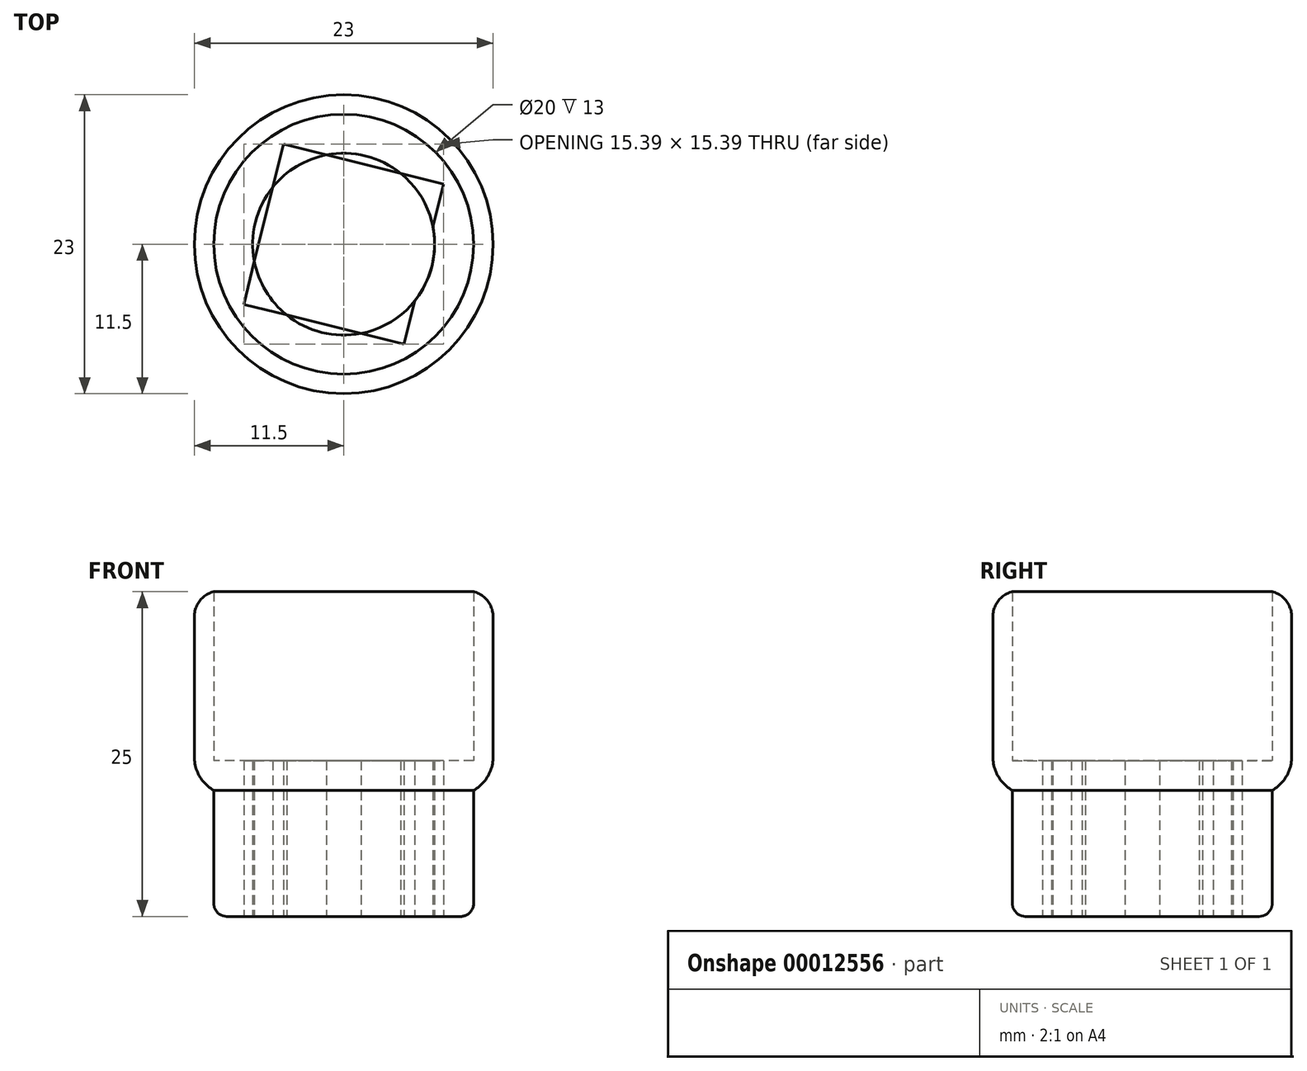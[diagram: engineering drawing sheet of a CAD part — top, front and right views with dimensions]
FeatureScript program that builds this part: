
annotation { "Feature Type Name" : "Feature", "Feature Type Description" : "" }
export const myFeature = defineFeature(function(context is Context, id is Id, definition is map)
    precondition{}
    {
        {
            var Q0;
            Q0=qCreatedBy(makeId("Top.planeOp"),FACE);
            var sketch = newSketch(context, id + "F0", { "sketchPlane" : qUnion([Q0])});
            skCircle(sketch, "E0", {"center": v(0, 0) * mm, "radius": 7 * mm});
            skCircle(sketch, "E1", {"center": v(0, 0) * mm, "radius": 10 * mm});
            skCircle(sketch, "E2", {"center": v(0, 0) * mm, "radius": 11.5 * mm});
            skCircle(sketch, "E3.cCircle", {"center": v(0, 0) * mm, "radius": 8.98 * mm, "construction": true});
            skLineSegment(sketch, "E3.0", {"start": v(7.7, 4.63) * mm, "end": v(4.63, -7.7) * mm});
            skLineSegment(sketch, "E3.1", {"start": v(4.63, -7.7) * mm, "end": v(-7.7, -4.63) * mm});
            skLineSegment(sketch, "E3.2", {"start": v(-7.7, -4.63) * mm, "end": v(-4.63, 7.7) * mm});
            skLineSegment(sketch, "E3.3", {"start": v(-4.63, 7.7) * mm, "end": v(7.7, 4.63) * mm});
            skSolve(sketch);
        }
        {
            var Q0;
            Q0=makeQuery(id+"F0.imprint","IMPRINT",FACE,{"disambiguationData":[TD([[makeQuery(id+"F0.imprint","IMPRINT",EDGE,{"derivedFrom":sQuery(id+"F0.wireOp",EDGE,"E1")}),1.0]])]});
            var Q1;
            {var subQ0=sQuery(id+"F0.wireOp",EDGE,"E3.3");var subQ1=sQuery(id+"F0.wireOp",EDGE,"E0");var subQ2=makeQuery(id+"F0.imprint","INTERSECT",VERTEX,{"disambiguationData":[OD(1.0)],"derivedFrom":[subQ1,subQ0]});Q1=makeQuery(id+"F0.imprint","IMPRINT",FACE,{"disambiguationData":[TD([[makeQuery(id+"F0.imprint","IMPRINT",EDGE,{"disambiguationData":[TD([[subQ2,-1.0]])],"derivedFrom":subQ1}),-1.0]])]});}
            var Q2;
            {var subQ0=sQuery(id+"F0.wireOp",EDGE,"E3.3");var subQ1=sQuery(id+"F0.wireOp",EDGE,"E0");var subQ2=makeQuery(id+"F0.imprint","INTERSECT",VERTEX,{"disambiguationData":[OD(0.0)],"derivedFrom":[subQ1,subQ0]});Q2=makeQuery(id+"F0.imprint","IMPRINT",FACE,{"disambiguationData":[TD([[makeQuery(id+"F0.imprint","IMPRINT",EDGE,{"disambiguationData":[TD([[subQ2,1.0]])],"derivedFrom":subQ1}),-1.0]])]});}
            var Q3;
            {var subQ0=sQuery(id+"F0.wireOp",EDGE,"E3.2");var subQ1=sQuery(id+"F0.wireOp",EDGE,"E0");var subQ2=makeQuery(id+"F0.imprint","INTERSECT",VERTEX,{"disambiguationData":[OD(1.0)],"derivedFrom":[subQ1,subQ0]});Q3=makeQuery(id+"F0.imprint","IMPRINT",FACE,{"disambiguationData":[TD([[makeQuery(id+"F0.imprint","IMPRINT",EDGE,{"disambiguationData":[TD([[subQ2,-1.0]])],"derivedFrom":subQ1}),-1.0]])]});}
            var Q4;
            {var subQ0=sQuery(id+"F0.wireOp",EDGE,"E3.1");var subQ1=sQuery(id+"F0.wireOp",EDGE,"E0");var subQ2=makeQuery(id+"F0.imprint","INTERSECT",VERTEX,{"disambiguationData":[OD(1.0)],"derivedFrom":[subQ1,subQ0]});Q4=makeQuery(id+"F0.imprint","IMPRINT",FACE,{"disambiguationData":[TD([[makeQuery(id+"F0.imprint","IMPRINT",EDGE,{"disambiguationData":[TD([[subQ2,-1.0]])],"derivedFrom":subQ1}),-1.0]])]});}
            extrude(context, id + "F1", {"entities" : qUnion([Q0, Q1, Q2, Q3, Q4]), "depth" : 12 * mm});
        }
        {
            var Q0;
            Q0=makeQuery(id+"F0.imprint","IMPRINT",FACE,{"disambiguationData":[TD([[makeQuery(id+"F0.imprint","IMPRINT",EDGE,{"derivedFrom":sQuery(id+"F0.wireOp",EDGE,"c6f08e52-6f51-46ba-8bd8-2db99310ce74")}),-1.0]])]});
            var Q1;
            Q1=makeQuery(id+"F0.imprint","IMPRINT",FACE,{"disambiguationData":[TD([[makeQuery(id+"F0.imprint","IMPRINT",EDGE,{"derivedFrom":sQuery(id+"F0.wireOp",EDGE,"E1")}),-1.0]])]});
            extrude(context, id + "F2", {"entities" : qUnion([Q0, Q1]), "operationType" : NewBodyOperationType.ADD, "depth" : 25 * mm, "hasSecondDirection" : true, "secondDirectionOppositeDirection" : false, "secondDirectionDepth" : 9.7 * mm});
        }
        {
            var Q0;
            {var subQ0=sQuery(id+"F0.wireOp",EDGE,"E3.2");var subQ1=sQuery(id+"F0.wireOp",EDGE,"E0");var subQ3=makeQuery(id+"F0.imprint","INTERSECT",VERTEX,{"disambiguationData":[OD(0.0)],"derivedFrom":[subQ1,subQ0]});Q0=makeQuery(id+"F0.imprint","IMPRINT",FACE,{"disambiguationData":[TD([[makeQuery(id+"F0.imprint","IMPRINT",EDGE,{"disambiguationData":[TD([[subQ3,-1.0]])],"derivedFrom":subQ1}),1.0]])]});}
            var Q1;
            {var subQ0=sQuery(id+"F0.wireOp",EDGE,"E3.3");var subQ1=sQuery(id+"F0.wireOp",EDGE,"E0");var subQ3=makeQuery(id+"F0.imprint","INTERSECT",VERTEX,{"disambiguationData":[OD(0.0)],"derivedFrom":[subQ1,subQ0]});Q1=makeQuery(id+"F0.imprint","IMPRINT",FACE,{"disambiguationData":[TD([[makeQuery(id+"F0.imprint","IMPRINT",EDGE,{"disambiguationData":[TD([[subQ3,-1.0]])],"derivedFrom":subQ1}),1.0]])]});}
            var Q2;
            {var subQ0=sQuery(id+"F0.wireOp",EDGE,"E3.0");var subQ1=sQuery(id+"F0.wireOp",EDGE,"E0");var subQ3=makeQuery(id+"F0.imprint","INTERSECT",VERTEX,{"disambiguationData":[OD(0.0)],"derivedFrom":[subQ1,subQ0]});Q2=makeQuery(id+"F0.imprint","IMPRINT",FACE,{"disambiguationData":[TD([[makeQuery(id+"F0.imprint","IMPRINT",EDGE,{"disambiguationData":[TD([[subQ3,1.0]])],"derivedFrom":subQ1}),1.0]])]});}
            var Q3;
            {var subQ0=sQuery(id+"F0.wireOp",EDGE,"E3.1");var subQ1=sQuery(id+"F0.wireOp",EDGE,"E0");var subQ3=makeQuery(id+"F0.imprint","INTERSECT",VERTEX,{"disambiguationData":[OD(0.0)],"derivedFrom":[subQ1,subQ0]});Q3=makeQuery(id+"F0.imprint","IMPRINT",FACE,{"disambiguationData":[TD([[makeQuery(id+"F0.imprint","IMPRINT",EDGE,{"disambiguationData":[TD([[subQ3,-1.0]])],"derivedFrom":subQ1}),1.0]])]});}
            extrude(context, id + "F3", {"entities" : qUnion([Q0, Q1, Q2, Q3]), "depth" : 12 * mm});
        }
        {
            var Q0;
            Q0=makeQuery(id+"F2.opExtrude","CAP_EDGE",EDGE,{"disambiguationData":[OSD([sQuery(id+"F0.wireOp",EDGE,"E2")])],"isStart":true});
            fillet(context, id + "F4", {"entities" : qUnion([Q0]), "radius" : 3 * mm, "tangentPropagation" : true, "allowEdgeOverflow" : false});
        }
        {
            var Q0;
            Q0=makeQuery(id+"F2.opExtrude","CAP_EDGE",EDGE,{"disambiguationData":[OSD([sQuery(id+"F0.wireOp",EDGE,"E2")])],"isStart":false});
            fillet(context, id + "F5", {"entities" : qUnion([Q0]), "radius" : 2 * mm, "tangentPropagation" : true, "allowEdgeOverflow" : false});
        }
        {
            var Q0;
            Q0=makeQuery(id+"F1.opExtrude","CAP_EDGE",EDGE,{"disambiguationData":[OSD([sQuery(id+"F0.wireOp",EDGE,"E1")])],"isStart":true});
            fillet(context, id + "F6", {"entities" : qUnion([Q0]), "radius" : 1 * mm, "tangentPropagation" : true, "allowEdgeOverflow" : false});
        }
    });
